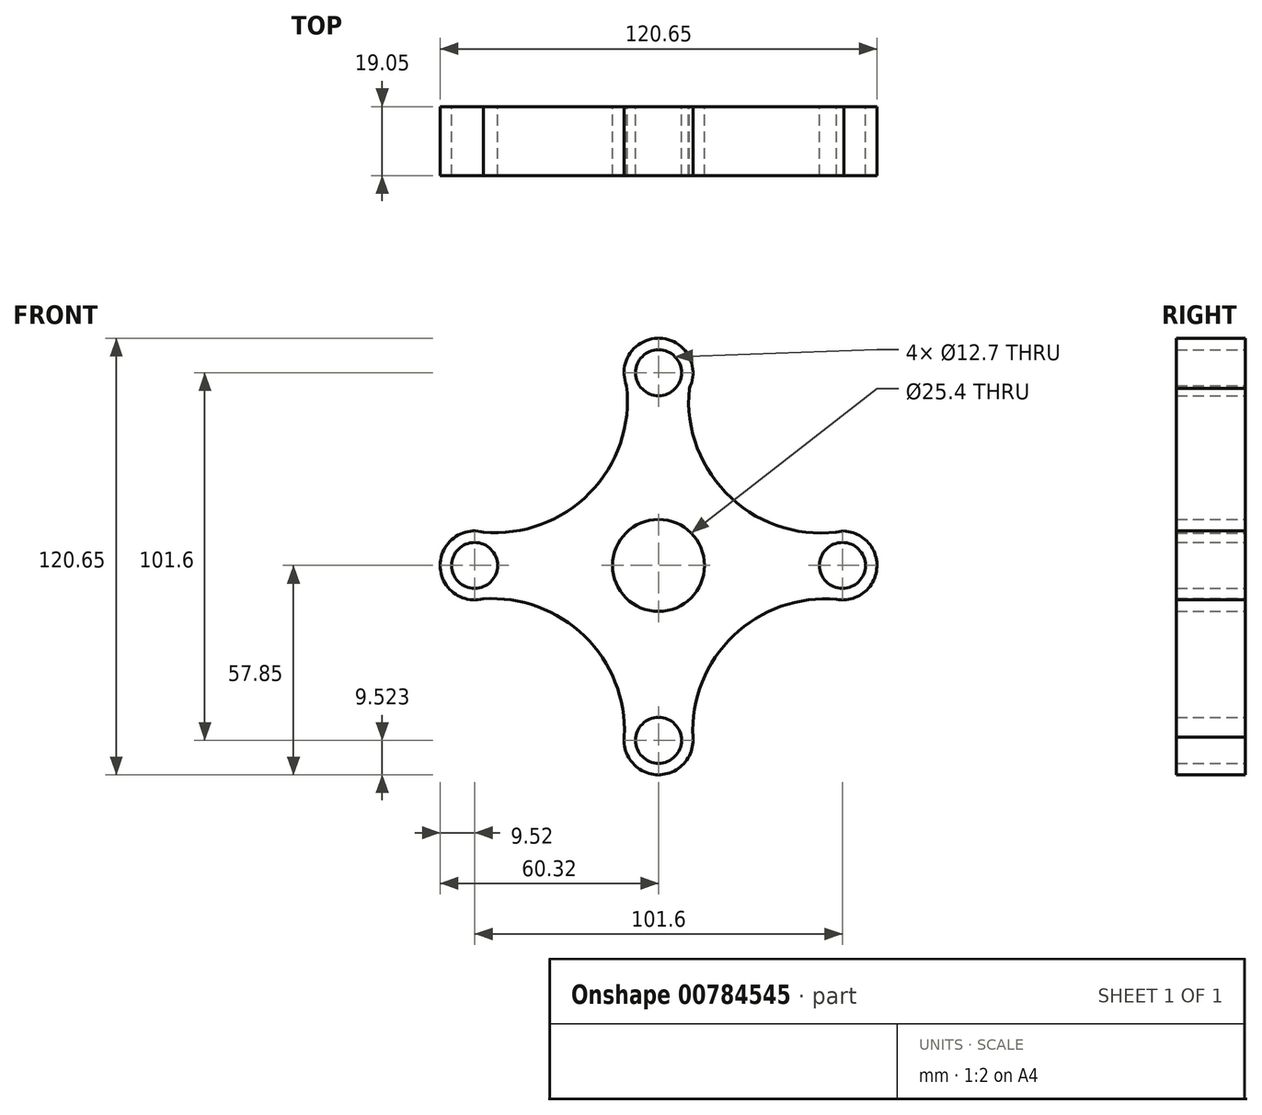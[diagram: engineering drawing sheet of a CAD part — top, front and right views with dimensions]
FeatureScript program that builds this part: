
annotation { "Feature Type Name" : "Feature", "Feature Type Description" : "" }
export const myFeature = defineFeature(function(context is Context, id is Id, definition is map)
    precondition{}
    {
        {
            var Q0;
            Q0=qCreatedBy(makeId("Front.planeOp"),FACE);
            var sketch = newSketch(context, id + "F0", { "sketchPlane" : qUnion([Q0])});
            skCircle(sketch, "E0", {"center": v(0, 53.27) * mm, "radius": 6.35 * mm});
            skCircle(sketch, "E1", {"center": v(50.8, 0) * mm, "radius": 6.35 * mm});
            skCircle(sketch, "E2", {"center": v(0, -48.33) * mm, "radius": 6.35 * mm});
            skCircle(sketch, "E3", {"center": v(-50.8, 0) * mm, "radius": 6.35 * mm});
            skArc(sketch, "E4", {"start": v(8.2, 48.42) * mm, "mid": v(0.7, 62.77) * mm, "end": v(-8.81, 49.66) * mm});
            skArc(sketch, "E5", {"start": v(49.18, -9.39) * mm, "mid": v(60.27, -0.99) * mm, "end": v(51.16, 9.52) * mm});
            skArc(sketch, "E6", {"start": v(-9.47, -47.26) * mm, "mid": v(-0.12, -57.85) * mm, "end": v(9.49, -47.5) * mm});
            skArc(sketch, "E7", {"start": v(-48.35, 9.2) * mm, "mid": v(-60.32, 0.05) * mm, "end": v(-48.45, -9.23) * mm});
            skArc(sketch, "E8", {"start": v(-50.91, 9.52) * mm, "mid": v(-18.44, 20.62) * mm, "end": v(-9.51, 53.75) * mm});
            skArc(sketch, "E9", {"start": v(9.45, 54.48) * mm, "mid": v(8.7, 51.48) * mm, "end": v(8.2, 48.42) * mm});
            skArc(sketch, "E10", {"start": v(-9.52, -48.28) * mm, "mid": v(-21.06, -18.93) * mm, "end": v(-51.16, -9.52) * mm});
            skArc(sketch, "E11", {"start": v(50.42, -9.52) * mm, "mid": v(20.9, -19.2) * mm, "end": v(9.52, -48.09) * mm});
            skArc(sketch, "E12", {"start": v(9.45, 54.48) * mm, "mid": v(18.06, 20.65) * mm, "end": v(51.16, 9.52) * mm});
            skCircle(sketch, "E13", {"center": v(0, 0) * mm, "radius": 12.7 * mm});
            skSolve(sketch);
        }
        {
            var Q0;
            Q0 = qSketchRegion(id + "F0", true);
            extrude(context, id + "F1", {"entities" : qUnion([Q0]), "depth" : 19.05 * mm, "offsetDistance" : 25.4 * mm});
        }
    });
